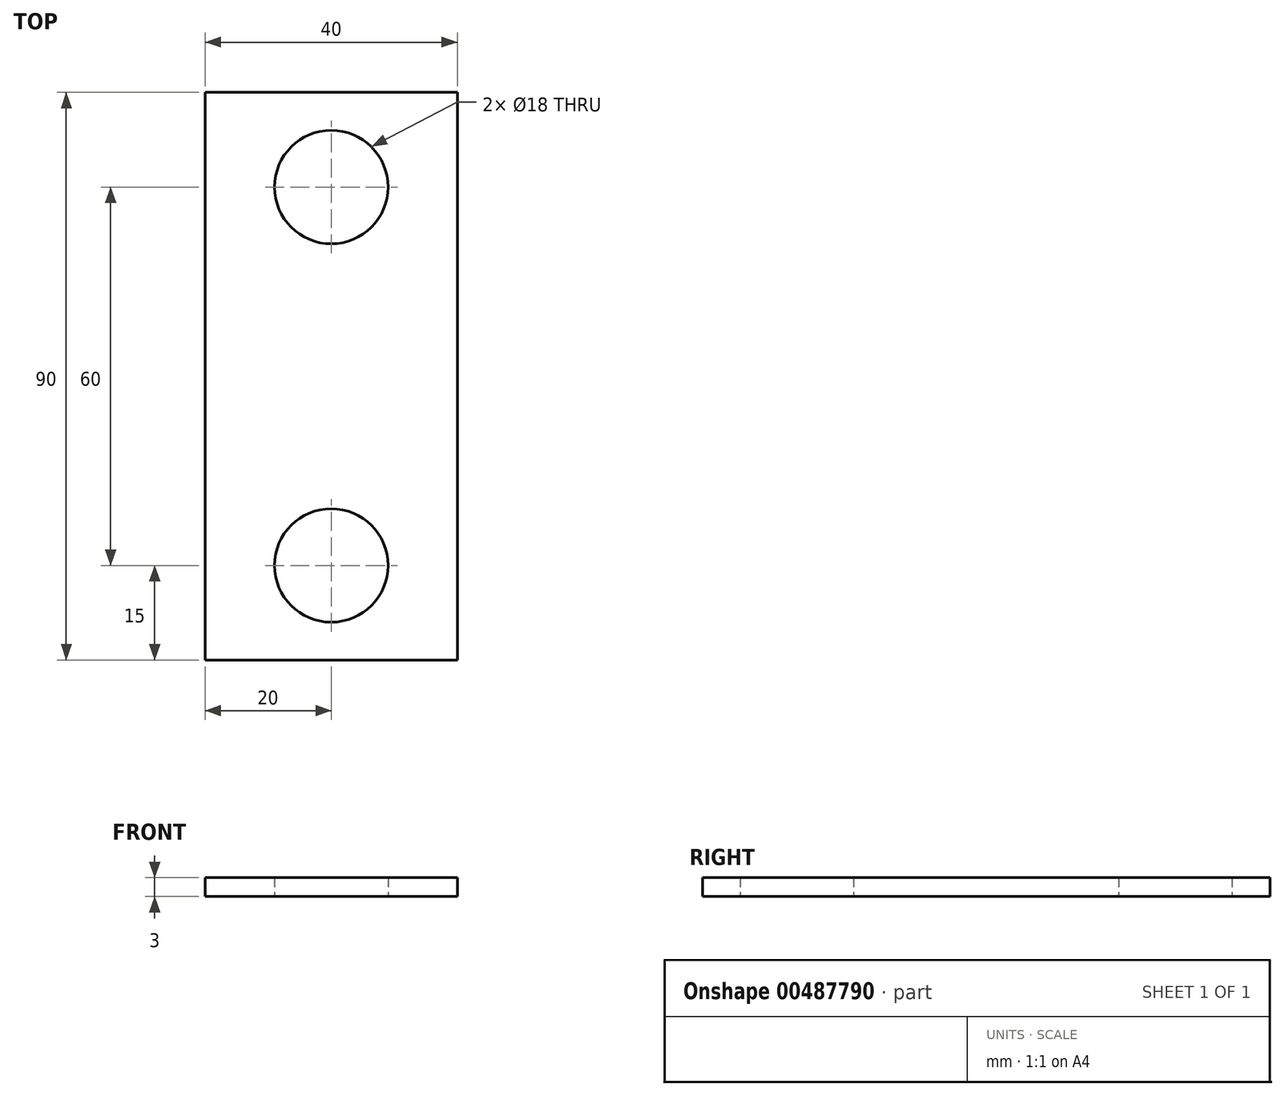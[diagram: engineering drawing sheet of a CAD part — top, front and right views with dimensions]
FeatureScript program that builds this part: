
annotation { "Feature Type Name" : "Feature", "Feature Type Description" : "" }
export const myFeature = defineFeature(function(context is Context, id is Id, definition is map)
    precondition{}
    {
        {
            var Q0;
            Q0=qCreatedBy(makeId("Top.planeOp"),FACE);
            var sketch = newSketch(context, id + "F0", { "sketchPlane" : qUnion([Q0])});
            skLineSegment(sketch, "E0.bottom", {"start": v(0, 0) * mm, "end": v(40, 0) * mm});
            skLineSegment(sketch, "E0.top", {"start": v(0, 90) * mm, "end": v(40, 90) * mm});
            skLineSegment(sketch, "E0.left", {"start": v(0, 0) * mm, "end": v(0, 90) * mm});
            skLineSegment(sketch, "E0.right", {"start": v(40, 0) * mm, "end": v(40, 90) * mm});
            skLineSegment(sketch, "E1", {"start": v(20, 90) * mm, "end": v(20, 0) * mm, "construction": true});
            skLineSegment(sketch, "E2", {"start": v(40, 45) * mm, "end": v(0, 45) * mm, "construction": true});
            skCircle(sketch, "E3", {"center": v(20, 75) * mm, "radius": 9 * mm});
            skCircle(sketch, "E4.MirrorC", {"center": v(20, 15) * mm, "radius": 9 * mm});
            skSolve(sketch);
        }
        {
            var Q0;
            Q0 = qSketchRegion(id + "F0", true);
            extrude(context, id + "F1", {"entities" : qUnion([Q0]), "depth" : 3 * mm});
        }
    });
